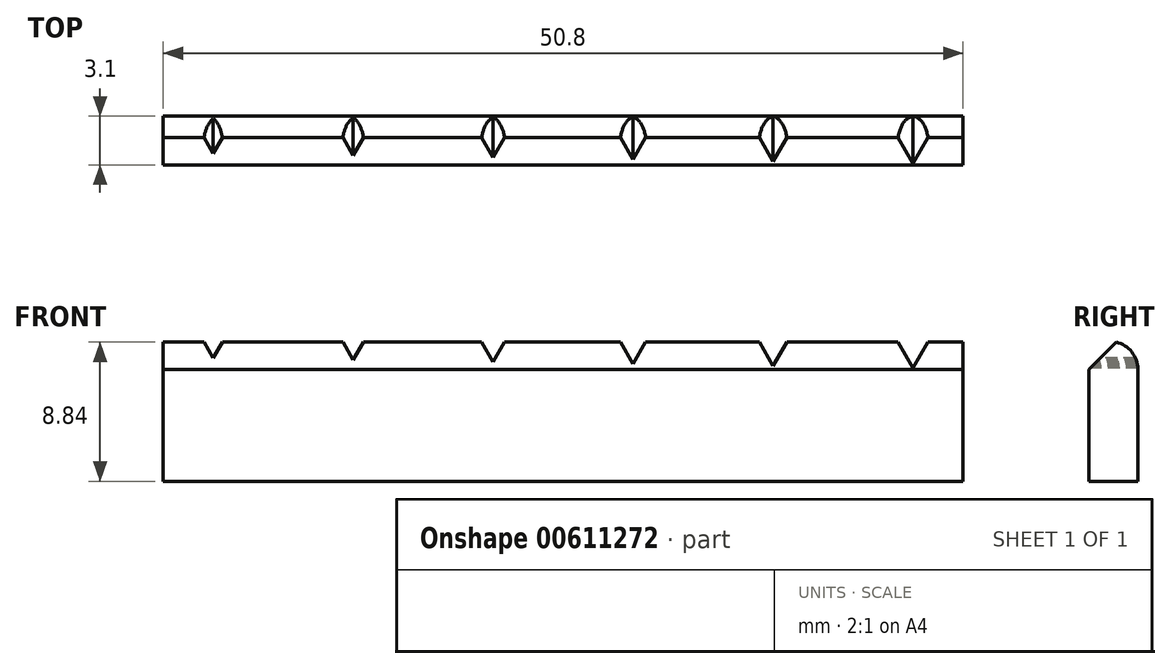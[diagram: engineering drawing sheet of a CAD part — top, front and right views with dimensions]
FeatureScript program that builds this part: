
annotation { "Feature Type Name" : "Feature", "Feature Type Description" : "" }
export const myFeature = defineFeature(function(context is Context, id is Id, definition is map)
    precondition{}
    {
        {
            var Q0;
            Q0=qCreatedBy(makeId("Top.planeOp"),FACE);
            var sketch = newSketch(context, id + "F0", { "sketchPlane" : qUnion([Q0])});
            skLineSegment(sketch, "E0.bottom", {"start": v(-25.4, 0) * mm, "end": v(25.4, 0) * mm});
            skLineSegment(sketch, "E0.top", {"start": v(-25.4, 3.1) * mm, "end": v(25.4, 3.1) * mm});
            skLineSegment(sketch, "E0.left", {"start": v(-25.4, 0) * mm, "end": v(-25.4, 3.1) * mm});
            skLineSegment(sketch, "E0.right", {"start": v(25.4, 0) * mm, "end": v(25.4, 3.1) * mm});
            skSolve(sketch);
        }
        {
            var Q0;
            Q0=makeQuery(id+"F0.imprint","IMPRINT",FACE,{"disambiguationData":[TD([[makeQuery(id+"F0.imprint","IMPRINT",EDGE,{"derivedFrom":sQuery(id+"F0.wireOp",EDGE,"E0.bottom")}),1.0]])]});
            extrude(context, id + "F1", {"entities" : qUnion([Q0]), "depth" : 8.9 * mm, "offsetDistance" : 25.4 * mm});
        }
        {
            var Q0;
            Q0=makeQuery(id+"F1.opExtrude","SWEPT_FACE",FACE,{"disambiguationData":[OSD([sQuery(id+"F0.wireOp",EDGE,"E0.bottom")])]});
            var sketch = newSketch(context, id + "F2", { "sketchPlane" : qUnion([Q0])});
            skCircle(sketch, "E1.cCircle", {"center": v(-22.22, 9.3) * mm, "radius": 0.73 * mm, "construction": true});
            skLineSegment(sketch, "E1.0", {"start": v(-20.95, 10.03) * mm, "end": v(-22.22, 7.83) * mm});
            skLineSegment(sketch, "E1.1", {"start": v(-22.22, 7.83) * mm, "end": v(-23.5, 10.03) * mm});
            skLineSegment(sketch, "E1.2", {"start": v(-23.5, 10.03) * mm, "end": v(-20.95, 10.03) * mm});
            skPoint(sketch, "E1.0.midPoint", {"position": v(-21.59, 8.93) * mm});
            skCircle(sketch, "E2.cCircle", {"center": v(-13.34, 9.17) * mm, "radius": 0.73 * mm, "construction": true});
            skLineSegment(sketch, "E2.0", {"start": v(-12.07, 9.9) * mm, "end": v(-13.34, 7.7) * mm});
            skLineSegment(sketch, "E2.1", {"start": v(-13.34, 7.7) * mm, "end": v(-14.6, 9.9) * mm});
            skLineSegment(sketch, "E2.2", {"start": v(-14.6, 9.9) * mm, "end": v(-12.07, 9.9) * mm});
            skPoint(sketch, "E2.0.midPoint", {"position": v(-12.7, 8.8) * mm});
            skCircle(sketch, "E3.cCircle", {"center": v(22.22, 8.66) * mm, "radius": 0.73 * mm, "construction": true});
            skLineSegment(sketch, "E3.0", {"start": v(23.5, 9.4) * mm, "end": v(22.22, 7.2) * mm});
            skLineSegment(sketch, "E3.1", {"start": v(22.22, 7.2) * mm, "end": v(20.95, 9.4) * mm});
            skLineSegment(sketch, "E3.2", {"start": v(20.96, 9.4) * mm, "end": v(23.5, 9.4) * mm});
            skPoint(sketch, "E3.0.midPoint", {"position": v(22.86, 8.3) * mm});
            skCircle(sketch, "E4.cCircle", {"center": v(13.33, 8.8) * mm, "radius": 0.73 * mm, "construction": true});
            skLineSegment(sketch, "E4.0", {"start": v(14.6, 9.53) * mm, "end": v(13.33, 7.33) * mm});
            skLineSegment(sketch, "E4.1", {"start": v(13.33, 7.33) * mm, "end": v(12.06, 9.52) * mm});
            skLineSegment(sketch, "E4.2", {"start": v(12.06, 9.53) * mm, "end": v(14.6, 9.53) * mm});
            skPoint(sketch, "E4.0.midPoint", {"position": v(13.97, 8.43) * mm});
            skLineSegment(sketch, "E5.0", {"start": v(-3.18, 9.78) * mm, "end": v(-4.45, 7.58) * mm});
            skLineSegment(sketch, "E5.1", {"start": v(-4.45, 7.58) * mm, "end": v(-5.72, 9.78) * mm});
            skLineSegment(sketch, "E5.2", {"start": v(-5.72, 9.78) * mm, "end": v(-3.18, 9.78) * mm});
            skLineSegment(sketch, "E6.0", {"start": v(5.72, 9.65) * mm, "end": v(4.45, 7.45) * mm});
            skLineSegment(sketch, "E6.1", {"start": v(4.45, 7.45) * mm, "end": v(3.18, 9.65) * mm});
            skLineSegment(sketch, "E6.2", {"start": v(3.18, 9.65) * mm, "end": v(5.72, 9.65) * mm});
            skSolve(sketch);
        }
        {
            var Q0;
            Q0=makeQuery(id+"F1.opExtrude","CAP_EDGE",EDGE,{"disambiguationData":[OSD([sQuery(id+"F0.wireOp",EDGE,"E0.top")])],"isStart":false});
            fillet(context, id + "F3", {"entities" : qUnion([Q0]), "radius" : 1.78 * mm, "tangentPropagation" : true, "allowEdgeOverflow" : false});
        }
        {
            var Q0;
            Q0=makeQuery(id+"F1.opExtrude","CAP_EDGE",EDGE,{"disambiguationData":[OSD([sQuery(id+"F0.wireOp",EDGE,"E0.bottom")])],"isStart":false});
            chamfer(context, id + "F4", {"entities" : qUnion([Q0]), "width" : 1.78 * mm, "tangentPropagation" : true});
        }
        {
            var Q0;
            {var subQ0=sQuery(id+"F2.wireOp",EDGE,"E1.1");var subQ1=sQuery(id+"F2.wireOp",EDGE,"E1.0");var subQ2=makeQuery(id+"F2.imprint","INTERSECT",VERTEX,{"derivedFrom":[subQ1,subQ0]});Q0=makeQuery(id+"F2.imprint","IMPRINT",FACE,{"disambiguationData":[TD([[makeQuery(id+"F2.imprint","IMPRINT",EDGE,{"disambiguationData":[TD([[subQ2,1.0]])],"derivedFrom":subQ1}),-1.0]])]});}
            var Q1;
            {var subQ0=sQuery(id+"F2.wireOp",EDGE,"E2.1");var subQ1=sQuery(id+"F2.wireOp",EDGE,"E2.0");var subQ2=makeQuery(id+"F2.imprint","INTERSECT",VERTEX,{"derivedFrom":[subQ1,subQ0]});Q1=makeQuery(id+"F2.imprint","IMPRINT",FACE,{"disambiguationData":[TD([[makeQuery(id+"F2.imprint","IMPRINT",EDGE,{"disambiguationData":[TD([[subQ2,1.0]])],"derivedFrom":subQ1}),-1.0]])]});}
            var Q2;
            {var subQ0=sQuery(id+"F2.wireOp",EDGE,"E4.1");var subQ1=sQuery(id+"F2.wireOp",EDGE,"E4.0");var subQ2=makeQuery(id+"F2.imprint","INTERSECT",VERTEX,{"derivedFrom":[subQ1,subQ0]});Q2=makeQuery(id+"F2.imprint","IMPRINT",FACE,{"disambiguationData":[TD([[makeQuery(id+"F2.imprint","IMPRINT",EDGE,{"disambiguationData":[TD([[subQ2,1.0]])],"derivedFrom":subQ1}),-1.0]])]});}
            var Q3;
            {var subQ0=sQuery(id+"F2.wireOp",EDGE,"E3.1");var subQ1=sQuery(id+"F2.wireOp",EDGE,"E3.0");var subQ2=makeQuery(id+"F2.imprint","INTERSECT",VERTEX,{"derivedFrom":[subQ1,subQ0]});Q3=makeQuery(id+"F2.imprint","IMPRINT",FACE,{"disambiguationData":[TD([[makeQuery(id+"F2.imprint","IMPRINT",EDGE,{"disambiguationData":[TD([[subQ2,1.0]])],"derivedFrom":subQ1}),-1.0]])]});}
            var Q4;
            {var subQ0=sQuery(id+"F2.wireOp",EDGE,"E5.1");var subQ1=sQuery(id+"F2.wireOp",EDGE,"E5.0");var subQ2=makeQuery(id+"F2.imprint","INTERSECT",VERTEX,{"derivedFrom":[subQ1,subQ0]});Q4=makeQuery(id+"F2.imprint","IMPRINT",FACE,{"disambiguationData":[TD([[makeQuery(id+"F2.imprint","IMPRINT",EDGE,{"disambiguationData":[TD([[subQ2,1.0]])],"derivedFrom":subQ1}),-1.0]])]});}
            var Q5;
            {var subQ0=sQuery(id+"F2.wireOp",EDGE,"E6.1");var subQ1=sQuery(id+"F2.wireOp",EDGE,"E6.0");var subQ2=makeQuery(id+"F2.imprint","INTERSECT",VERTEX,{"derivedFrom":[subQ1,subQ0]});Q5=makeQuery(id+"F2.imprint","IMPRINT",FACE,{"disambiguationData":[TD([[makeQuery(id+"F2.imprint","IMPRINT",EDGE,{"disambiguationData":[TD([[subQ2,1.0]])],"derivedFrom":subQ1}),-1.0]])]});}
            extrude(context, id + "F5", {"entities" : qUnion([Q0, Q1, Q2, Q3, Q4, Q5]), "operationType" : NewBodyOperationType.REMOVE, "oppositeDirection" : true, "depth" : 25.4 * mm, "offsetDistance" : 25.4 * mm});
        }
    });
